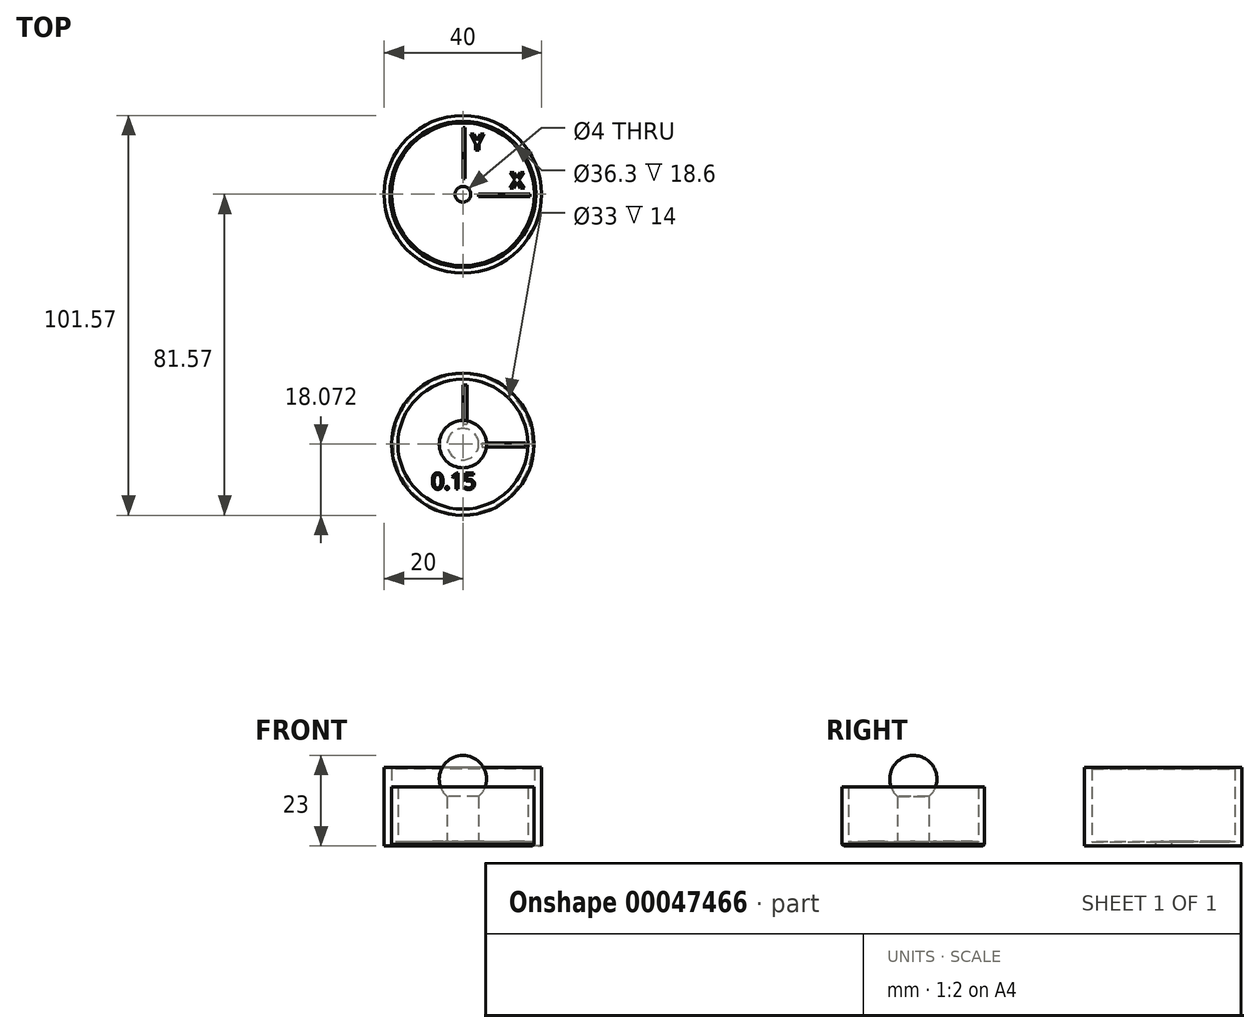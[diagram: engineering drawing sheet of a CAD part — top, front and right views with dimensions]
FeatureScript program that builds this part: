
annotation { "Feature Type Name" : "Feature", "Feature Type Description" : "" }
export const myFeature = defineFeature(function(context is Context, id is Id, definition is map)
    precondition{}
    {
        {
            var Q0;
            Q0=qCreatedBy(makeId("Top.planeOp"),FACE);
            var sketch = newSketch(context, id + "F0", { "sketchPlane" : qUnion([Q0])});
            skCircle(sketch, "E0", {"center": v(0, 0) * mm, "radius": 20 * mm});
            skCircle(sketch, "E1", {"center": v(0, 0) * mm, "radius": 18.15 * mm});
            skCircle(sketch, "E2", {"center": v(0, -63.5) * mm, "radius": 18.07 * mm});
            skCircle(sketch, "E3", {"center": v(0, -63.5) * mm, "radius": 16.5 * mm});
            skCircle(sketch, "E4", {"center": v(0, 0) * mm, "radius": 2 * mm});
            skCircle(sketch, "E5", {"center": v(0, -63.5) * mm, "radius": 4 * mm});
            skSolve(sketch);
        }
        {
            var Q0;
            Q0=makeQuery(id+"F0.imprint","IMPRINT",FACE,{"disambiguationData":[TD([[makeQuery(id+"F0.imprint","IMPRINT",EDGE,{"derivedFrom":sQuery(id+"F0.wireOp",EDGE,"E1")}),1.0]])]});
            var Q1;
            Q1=makeQuery(id+"F0.imprint","IMPRINT",FACE,{"disambiguationData":[TD([[makeQuery(id+"F0.imprint","IMPRINT",EDGE,{"derivedFrom":sQuery(id+"F0.wireOp",EDGE,"E3")}),1.0]])]});
            extrude(context, id + "F1", {"entities" : qUnion([Q0, Q1]), "depth" : 1 * mm});
        }
        {
            var Q0;
            Q0=makeQuery(id+"F0.imprint","IMPRINT",FACE,{"disambiguationData":[TD([[makeQuery(id+"F0.imprint","IMPRINT",EDGE,{"derivedFrom":sQuery(id+"F0.wireOp",EDGE,"E0")}),1.0]])]});
            extrude(context, id + "F2", {"entities" : qUnion([Q0]), "operationType" : NewBodyOperationType.ADD, "depth" : 20 * mm});
        }
        {
            var Q0;
            Q0=makeQuery(id+"F0.imprint","IMPRINT",FACE,{"disambiguationData":[TD([[makeQuery(id+"F0.imprint","IMPRINT",EDGE,{"derivedFrom":sQuery(id+"F0.wireOp",EDGE,"E2")}),1.0]])]});
            extrude(context, id + "F3", {"entities" : qUnion([Q0]), "operationType" : NewBodyOperationType.ADD, "depth" : 15 * mm});
        }
        {
            var Q0;
            Q0=makeQuery(id+"F0.imprint","IMPRINT",FACE,{"disambiguationData":[TD([[makeQuery(id+"F0.imprint","IMPRINT",EDGE,{"derivedFrom":sQuery(id+"F0.wireOp",EDGE,"E5")}),1.0]])]});
            extrude(context, id + "F4", {"entities" : qUnion([Q0]), "operationType" : NewBodyOperationType.ADD, "depth" : 17 * mm});
        }
        {
            var Q0;
            Q0=makeQuery(id+"F2.opExtrude","CAP_EDGE",EDGE,{"disambiguationData":[OSD([sQuery(id+"F0.wireOp",EDGE,"E1")])],"isStart":false});
            chamfer(context, id + "F5", {"entities" : qUnion([Q0]), "width" : 0.4 * mm});
        }
        {
            var Q0;
            Q0=makeQuery(id+"F1.opExtrude","CAP_FACE",FACE,{"disambiguationData":[OSD([sQuery(id+"F0.wireOp",EDGE,"E1"),sQuery(id+"F0.wireOp",EDGE,"E4")])],"isStart":false});
            var sketch = newSketch(context, id + "F6", { "sketchPlane" : qUnion([Q0])});
            skLineSegment(sketch, "E6.bottom", {"start": v(0, 17) * mm, "end": v(0.6, 17) * mm});
            skLineSegment(sketch, "E6.top", {"start": v(0, 4) * mm, "end": v(0.6, 4) * mm});
            skLineSegment(sketch, "E6.left", {"start": v(0, 17) * mm, "end": v(0, 4) * mm});
            skLineSegment(sketch, "E6.right", {"start": v(0.6, 17) * mm, "end": v(0.6, 4) * mm});
            skLineSegment(sketch, "E7.bottom", {"start": v(4, 0) * mm, "end": v(17, 0) * mm});
            skLineSegment(sketch, "E7.top", {"start": v(4, -0.6) * mm, "end": v(17, -0.6) * mm});
            skLineSegment(sketch, "E7.left", {"start": v(4, 0) * mm, "end": v(4, -0.6) * mm});
            skLineSegment(sketch, "E7.right", {"start": v(17, 0) * mm, "end": v(17, -0.6) * mm});
            skText(sketch, "E8", { "text": "X", "fontName": "OpenSans-Bold.ttf"});
            skText(sketch, "E9", { "text": "Y", "fontName": "OpenSans-Bold.ttf"});
            const initialGuessF6  = {"E8": [0.01192, 0.00161, 1, 0, 0.004], "E9": [0.0019, 0.01127, 1, 0, 0.004]};
            skSetInitialGuess(sketch, initialGuessF6);
            skSolve(sketch);
        }
        {
            var Q0;
            Q0 = qSketchRegion(id + "F6", true);
            extrude(context, id + "F7", {"entities" : qUnion([Q0]), "operationType" : NewBodyOperationType.ADD, "depth" : 0.2 * mm});
        }
        {
            var Q0;
            Q0=makeQuery(id+"F1.opExtrude","CAP_FACE",FACE,{"disambiguationData":[OSD([sQuery(id+"F0.wireOp",EDGE,"E3"),sQuery(id+"F0.wireOp",EDGE,"E5")])],"isStart":false});
            var sketch = newSketch(context, id + "F8", { "sketchPlane" : qUnion([Q0])});
            skLineSegment(sketch, "E10.bottom", {"start": v(0, -48.42) * mm, "end": v(1.1, -48.42) * mm});
            skLineSegment(sketch, "E10.top", {"start": v(0, -58.4) * mm, "end": v(1.1, -58.4) * mm});
            skLineSegment(sketch, "E10.left", {"start": v(0, -48.42) * mm, "end": v(0, -58.4) * mm});
            skLineSegment(sketch, "E10.right", {"start": v(1.1, -48.42) * mm, "end": v(1.1, -58.4) * mm});
            skLineSegment(sketch, "E11.bottom", {"start": v(4.89, -63.14) * mm, "end": v(15.87, -63.14) * mm});
            skLineSegment(sketch, "E11.top", {"start": v(4.89, -64.19) * mm, "end": v(15.87, -64.19) * mm});
            skLineSegment(sketch, "E11.left", {"start": v(4.89, -63.14) * mm, "end": v(4.89, -64.19) * mm});
            skLineSegment(sketch, "E11.right", {"start": v(15.87, -63.14) * mm, "end": v(15.87, -64.19) * mm});
            skText(sketch, "E12", { "text": "0.15", "fontName": "OpenSans-Regular.ttf"});
            const initialGuessF8  = {"E12": [-0.00805, -0.07493, 1, 0, 0.00412]};
            skSetInitialGuess(sketch, initialGuessF8);
            skSolve(sketch);
        }
        {
            var Q0;
            Q0 = qSketchRegion(id + "F8", true);
            extrude(context, id + "F9", {"entities" : qUnion([Q0]), "operationType" : NewBodyOperationType.ADD, "depth" : 0.2 * mm});
        }
        {
            var Q0;
            Q0=makeQuery(id+"F3.opExtrude","CAP_EDGE",EDGE,{"disambiguationData":[OSD([sQuery(id+"F0.wireOp",EDGE,"E2")])],"isStart":true});
            chamfer(context, id + "F10", {"entities" : qUnion([Q0]), "width" : 0.4 * mm, "tangentPropagation" : true});
        }
        {
            var Q0;
            Q0=makeQuery(id+"F4.opExtrude","CAP_FACE",FACE,{"disambiguationData":[OSD([sQuery(id+"F0.wireOp",EDGE,"E5")])],"isStart":false});
            var sketch = newSketch(context, id + "F11", { "sketchPlane" : qUnion([Q0])});
            skLineSegment(sketch, "E13", {"start": v(-23.65, -63.5) * mm, "end": v(-6, -63.5) * mm, "construction": true});
            skLineSegment(sketch, "E14", {"start": v(-6, -63.5) * mm, "end": v(25.47, -63.5) * mm, "construction": true});
            skArc(sketch, "E15", {"start": v(-6, -63.5) * mm, "mid": v(0, -69.5) * mm, "end": v(6, -63.5) * mm});
            skLineSegment(sketch, "E16", {"start": v(-6, -63.5) * mm, "end": v(6, -63.5) * mm});
            skSolve(sketch);
        }
        {
            var Q0;
            {var subQ0=sQuery(id+"F11.wireOp",EDGE,"E15");Q0=makeQuery(id+"F11.imprint","IMPRINT",FACE,{"disambiguationData":[TD([[makeQuery(id+"F11.imprint","IMPRINT",EDGE,{"derivedFrom":subQ0}),1.0]])]});}
            var Q1;
            {var subQ0=sQuery(id+"F11.wireOp",EDGE,"E16");var subQ1=makeQuery(id+"F4.opExtrude","CAP_EDGE",EDGE,{"disambiguationData":[OSD([sQuery(id+"F0.wireOp",EDGE,"E5")])],"isStart":false});var subQ2=makeQuery(id+"F11.imprint","INTERSECT",VERTEX,{"disambiguationData":[OD(0.0)],"derivedFrom":[subQ1,subQ0]});Q1=makeQuery(id+"F11.imprint","IMPRINT",FACE,{"disambiguationData":[TD([[makeQuery(id+"F11.imprint","IMPRINT",EDGE,{"disambiguationData":[TD([[subQ2,-1.0]])],"derivedFrom":subQ0}),-1.0]])]});}
            var Q2;
            Q2=sQuery(id+"F11.wireOp",EDGE,"E15");
            var Q3;
            Q3=sQuery(id+"F11.wireOp",EDGE,"E13");
            revolve(context, id + "F12", {"operationType" : NewBodyOperationType.ADD, "entities" : qUnion([Q0, Q1]), "surfaceEntities" : qUnion([Q2]), "axis" : qUnion([Q3]), "revolveType" : RevolveType.FULL});
        }
    });
